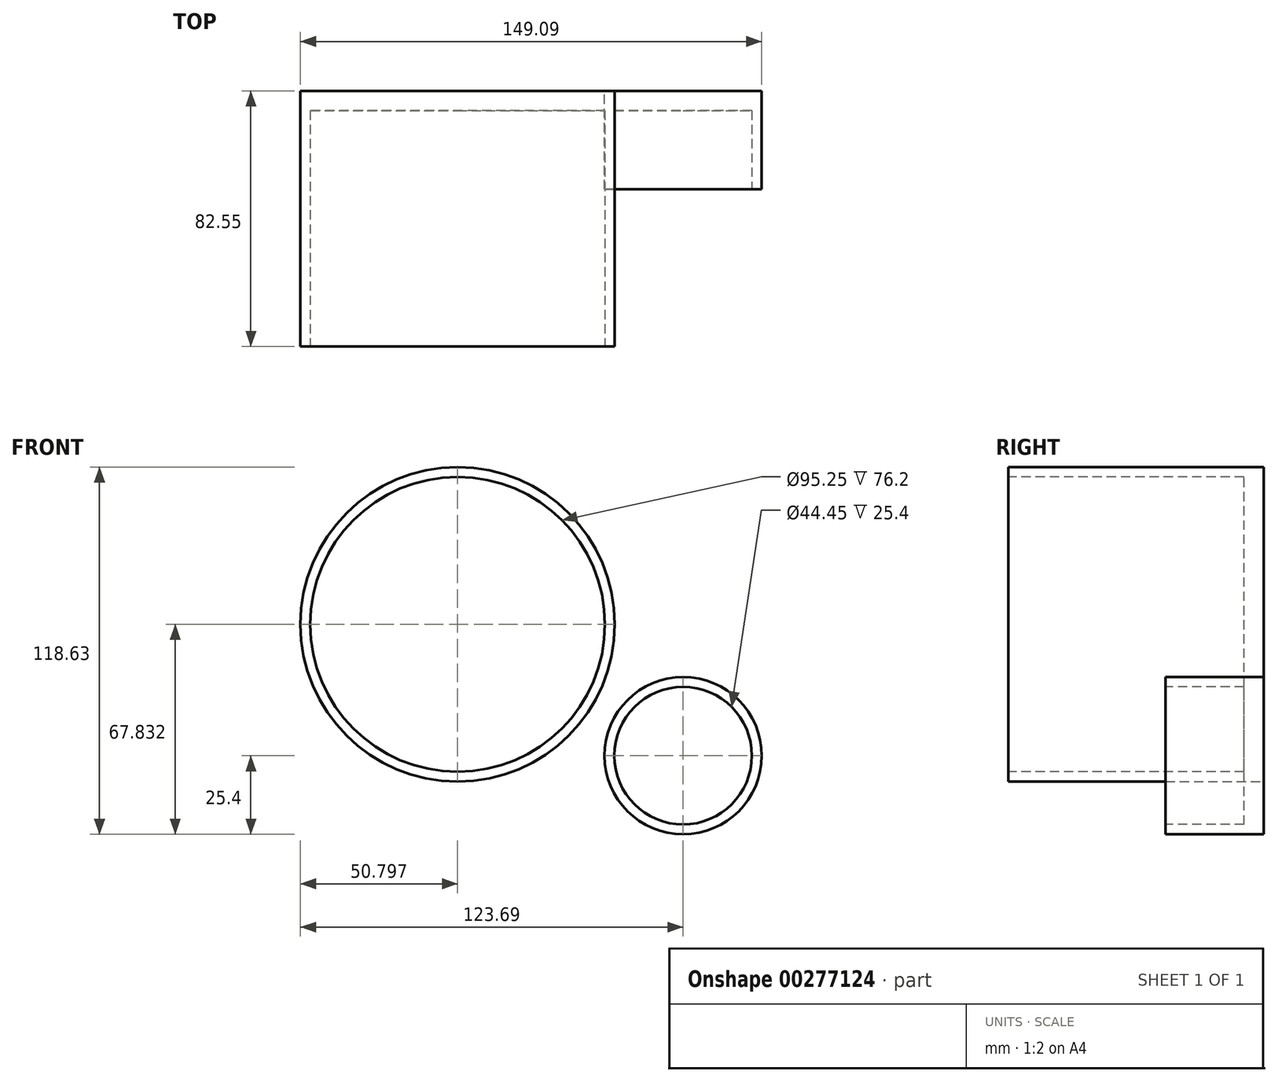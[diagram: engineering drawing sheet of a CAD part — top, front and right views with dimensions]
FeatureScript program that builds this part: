
annotation { "Feature Type Name" : "Feature", "Feature Type Description" : "" }
export const myFeature = defineFeature(function(context is Context, id is Id, definition is map)
    precondition{}
    {
        {
            var Q0;
            Q0=qCreatedBy(makeId("Front.planeOp"),FACE);
            var sketch = newSketch(context, id + "F0", { "sketchPlane" : qUnion([Q0])});
            skCircle(sketch, "E0", {"center": v(-42.13, 10.18) * mm, "radius": 50.8 * mm});
            skSolve(sketch);
        }
        {
            var Q0;
            Q0=qCreatedBy(makeId("Front.planeOp"),FACE);
            var sketch = newSketch(context, id + "F1", { "sketchPlane" : qUnion([Q0])});
            skCircle(sketch, "E1", {"center": v(30.76, -32.25) * mm, "radius": 25.4 * mm});
            skSolve(sketch);
        }
        {
            var Q0;
            Q0=makeQuery(id+"F0.imprint","IMPRINT",FACE,{"disambiguationData":[TD([[makeQuery(id+"F0.imprint","IMPRINT",EDGE,{"derivedFrom":sQuery(id+"F0.wireOp",EDGE,"E0")}),1.0]])]});
            extrude(context, id + "F2", {"entities" : qUnion([Q0]), "depth" : 82.55 * mm});
        }
        {
            var Q0;
            Q0=makeQuery(id+"F1.imprint","IMPRINT",FACE,{"disambiguationData":[TD([[makeQuery(id+"F1.imprint","IMPRINT",EDGE,{"derivedFrom":sQuery(id+"F1.wireOp",EDGE,"E1")}),1.0]])]});
            extrude(context, id + "F3", {"entities" : qUnion([Q0]), "depth" : 31.75 * mm});
        }
        {
            var Q0;
            Q0=makeQuery(id+"F2.opExtrude","CAP_FACE",FACE,{"disambiguationData":[OSD([sQuery(id+"F0.wireOp",EDGE,"E0")])],"isStart":false});
            var sketch = newSketch(context, id + "F4", { "sketchPlane" : qUnion([Q0])});
            skCircle(sketch, "E2", {"center": v(-42.13, 10.18) * mm, "radius": 47.63 * mm});
            skSolve(sketch);
        }
        {
            var Q0;
            Q0=makeQuery(id+"F4.imprint","IMPRINT",FACE,{"disambiguationData":[TD([[makeQuery(id+"F4.imprint","IMPRINT",EDGE,{"derivedFrom":sQuery(id+"F4.wireOp",EDGE,"E2")}),1.0]])]});
            extrude(context, id + "F5", {"entities" : qUnion([Q0]), "operationType" : NewBodyOperationType.REMOVE, "oppositeDirection" : true, "depth" : 76.2 * mm});
        }
        {
            var Q0;
            Q0=makeQuery(id+"F3.opExtrude","CAP_FACE",FACE,{"disambiguationData":[OSD([sQuery(id+"F1.wireOp",EDGE,"E1")])],"isStart":false});
            var sketch = newSketch(context, id + "F6", { "sketchPlane" : qUnion([Q0])});
            skCircle(sketch, "E3", {"center": v(30.76, -32.25) * mm, "radius": 22.23 * mm});
            skSolve(sketch);
        }
        {
            var Q0;
            Q0=makeQuery(id+"F6.imprint","IMPRINT",FACE,{"disambiguationData":[TD([[makeQuery(id+"F6.imprint","IMPRINT",EDGE,{"derivedFrom":sQuery(id+"F6.wireOp",EDGE,"E3")}),1.0]])]});
            extrude(context, id + "F7", {"entities" : qUnion([Q0]), "operationType" : NewBodyOperationType.REMOVE, "oppositeDirection" : true, "depth" : 25.4 * mm});
        }
    });
